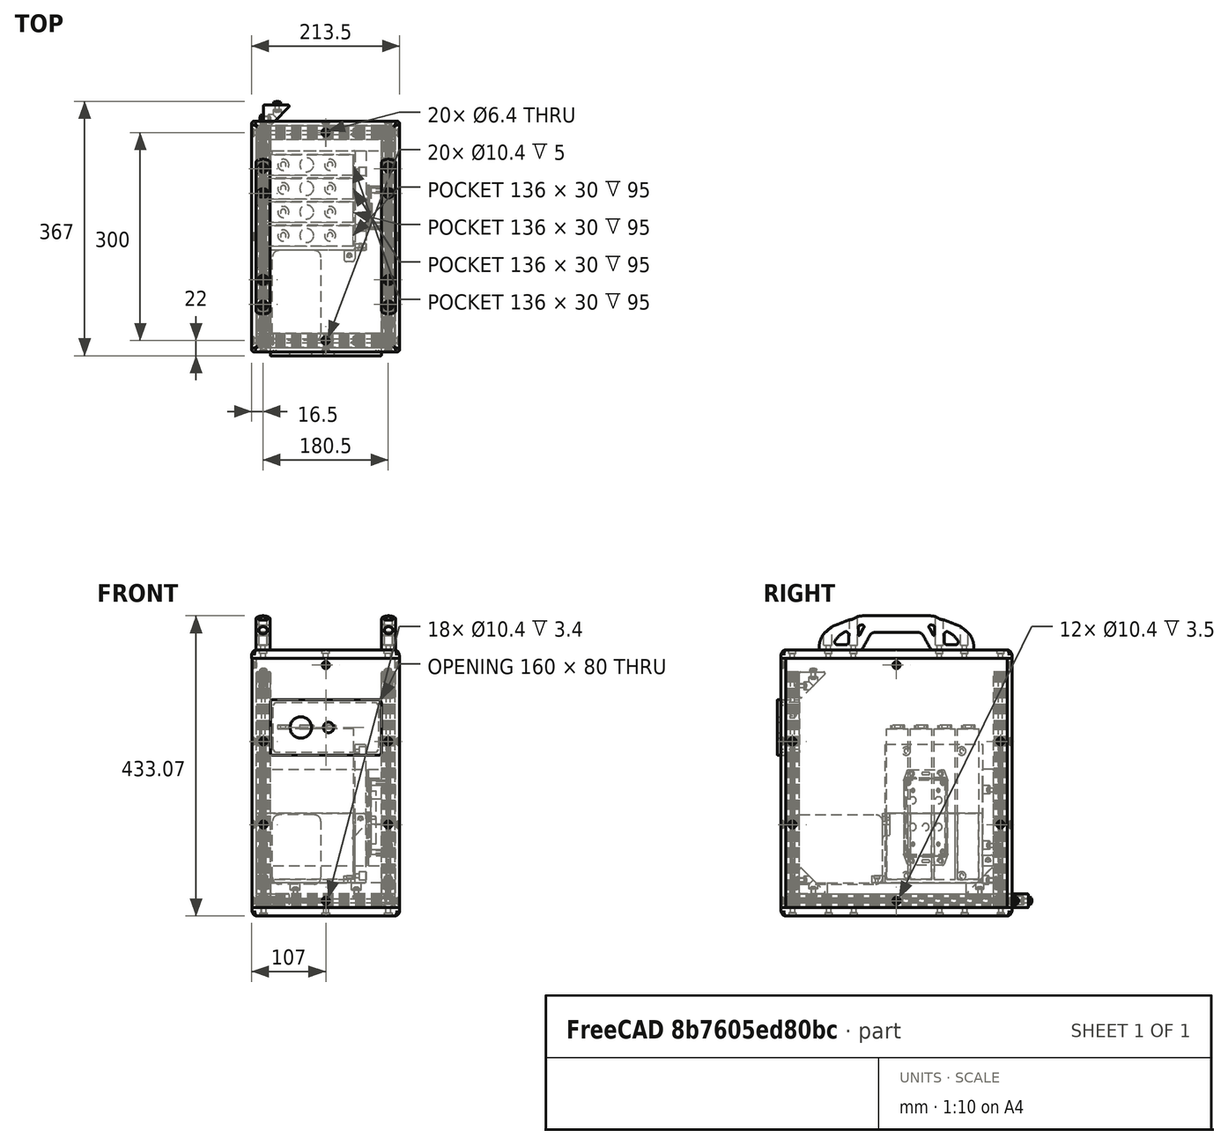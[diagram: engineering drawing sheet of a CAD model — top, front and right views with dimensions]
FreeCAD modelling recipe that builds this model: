
FCSTD DOCUMENT  (FreeCAD 0.17R9796 (Git))
Label: UPKframeNG2j
License: All rights reserved
LicenseURL: http://en.wikipedia.org/wiki/All_rights_reserved
objects: Part::Feature×74, Part::FeaturePython×24, Part::Compound×12, App::FeaturePython×8, App::Part×6, Part::Cylinder×5, Part::Box×4, Part::Cut×4, PartDesign::Body×2, PartDesign::Pocket×1, Part::Fillet×1, Part::MultiFuse×1
note: 129 computed .brp shape members not serialized (recipe doc carries the construction recipe); baked Part::Feature solids carry a one-line shape summary decoded from their .brp

FEATURE [Part::Feature] Pocket003001  label="tslot32con"
  Placement = pos=(0,10,10) rot=(1,0,0;1.5708rad)
  shape: bbox 20 x 320 x 20 mm, 150 faces (baked)
FEATURE [Part::Feature] Pocket003002  label="tslot16"
  Placement = pos=(10,0,10) rot=(0,1,0;1.5708rad)
  shape: bbox 160 x 20 x 20 mm, 94 faces (baked)
FEATURE [Part::Feature] Pocket003006  label="tslot16_001"
  Placement = pos=(10,-300,10) rot=(0,1,0;1.5708rad)
  shape: bbox 160 x 20 x 20 mm, 94 faces (baked)
FEATURE [Part::Feature] Pocket003007  label="tslot32con_001"
  Placement = pos=(180,-310,10) rot=(0,0.707107,0.707107;3.14159rad)
  shape: bbox 20 x 320 x 20 mm, 150 faces (baked)
FEATURE [Part::FeaturePython] Screw  label="M6x25-Screw"  # Fasteners workbench fastener (typed FeaturePython)
  Placement = pos=(-4,0,10) rot=(0,-1,0;1.5708rad)
  diameter = 7
  invert = false
  length = 6
  matchOuter = false
  offset = 0
  thread = false
  type = 15
FEATURE [Part::FeaturePython] Screw001  label="M6x25-Screw004"  # Fasteners workbench fastener (typed FeaturePython)
  Placement = pos=(-4,-300,10) rot=(0,-1,0;1.5708rad)
  diameter = 7
  invert = false
  length = 6
  matchOuter = false
  offset = 0
  thread = false
  type = 15
FEATURE [Part::FeaturePython] Screw002  label="M6x25-Screw005"  # Fasteners workbench fastener (typed FeaturePython)
  Placement = pos=(184,0,10) rot=(0,1,0;1.5708rad)
  diameter = 7
  invert = false
  length = 6
  matchOuter = false
  offset = 0
  thread = false
  type = 15
FEATURE [Part::FeaturePython] Screw004  label="M6x25-Screw006"  # Fasteners workbench fastener (typed FeaturePython)
  Placement = pos=(184,-300,10) rot=(0,1,0;1.5708rad)
  diameter = 7
  invert = false
  length = 6
  matchOuter = false
  offset = 0
  thread = false
  type = 15
FEATURE [App::Part] Part  label="lower_frame"
  Group = -> [Pocket003001,Pocket003002,Pocket003006,Pocket003007,Screw,Screw001,Screw002,Screw004]
  License = CC BY 3.0
  LicenseURL = http://creativecommons.org/licenses/by/3.0/
  Origin = -> PartOrigin
FEATURE [Part::Feature] Pocket003008  label="tslot32con001"
  Placement = pos=(0,10,10) rot=(1,0,0;1.5708rad)
  shape: bbox 20 x 320 x 20 mm, 150 faces (baked)
FEATURE [Part::Feature] Pocket003009  label="tslot041"
  Placement = pos=(10,0,10) rot=(0,1,0;1.5708rad)
  shape: bbox 160 x 20 x 20 mm, 94 faces (baked)
FEATURE [Part::Feature] Pocket003010  label="tslot16_002"
  Placement = pos=(10,-300,10) rot=(0,1,0;1.5708rad)
  shape: bbox 160 x 20 x 20 mm, 94 faces (baked)
FEATURE [Part::Feature] Pocket003011  label="tslot32con_002"
  Placement = pos=(180,-310,10) rot=(0,0.707107,0.707107;3.14159rad)
  shape: bbox 20 x 320 x 20 mm, 150 faces (baked)
FEATURE [Part::FeaturePython] Screw005  label="M6x25-Screw007"  # Fasteners workbench fastener (typed FeaturePython)
  Placement = pos=(-4,0,10) rot=(0,-1,0;1.5708rad)
  diameter = 7
  invert = false
  length = 6
  matchOuter = false
  offset = 0
  thread = false
  type = 15
FEATURE [Part::FeaturePython] Screw006  label="M6x25-Screw008"  # Fasteners workbench fastener (typed FeaturePython)
  Placement = pos=(-4,-300,10) rot=(0,-1,0;1.5708rad)
  diameter = 7
  invert = false
  length = 6
  matchOuter = false
  offset = 0
  thread = false
  type = 15
FEATURE [Part::FeaturePython] Screw007  label="M6x25-Screw009"  # Fasteners workbench fastener (typed FeaturePython)
  Placement = pos=(184,0,10) rot=(0,1,0;1.5708rad)
  diameter = 7
  invert = false
  length = 6
  matchOuter = false
  offset = 0
  thread = false
  type = 15
FEATURE [Part::FeaturePython] Screw008  label="M6x25-Screw010"  # Fasteners workbench fastener (typed FeaturePython)
  Placement = pos=(184,-300,10) rot=(0,1,0;1.5708rad)
  diameter = 7
  invert = false
  length = 6
  matchOuter = false
  offset = 0
  thread = false
  type = 15
FEATURE [App::Part] Part001  label="upper_frame"
  Group = -> [Pocket003008,Pocket003009,Pocket003010,Pocket003011,Screw005,Screw006,Screw007,Screw008]
  License = CC BY 3.0
  LicenseURL = http://creativecommons.org/licenses/by/3.0/
  Origin = -> PartOrigin001
  Placement = pos=(0,0,340) rot=(0,0,1;0rad)
FEATURE [Part::Feature] Fillet004001  label="Fillet005"
  shape: bbox 37.5 x 37.5 x 20 mm, 26 faces (baked)
FEATURE [Part::FeaturePython] Screw009  label="M6x12-Screw"  # Fasteners workbench fastener (typed FeaturePython)
  Placement = pos=(7,20,10) rot=(0,1,0;1.5708rad)
  diameter = 4
  invert = false
  length = 1
  matchOuter = false
  offset = 0
  thread = false
  type = 20
FEATURE [Part::Feature] Body001  label="m6nutplate"
  Placement = pos=(-1.5,15,5) rot=(0,-1,0;1.5708rad)
  shape: bbox 3 x 10 x 10 mm, 9 faces (baked)
FEATURE [App::Part] Part002  label="cornerstonescrewnut"
  License = CC BY 3.0
  LicenseURL = http://creativecommons.org/licenses/by/3.0/
  Origin = -> PartOrigin002
  Placement = pos=(10,-50,20) rot=(0,-1,0;1.5708rad)
FEATURE [Part::FeaturePython] Screw010  label="M6x12-Screw001"  # Fasteners workbench fastener (typed FeaturePython)
  Placement = pos=(20,33,10) rot=(1,0,0;1.5708rad)
  diameter = 4
  invert = false
  length = 1
  matchOuter = false
  offset = 0
  thread = false
  type = 20
FEATURE [Part::Feature] Body002  label="m6nutplate001"
  Placement = pos=(15,41.5,5) rot=(0.57735,0.57735,0.57735;4.18879rad)
  shape: bbox 10 x 3 x 10 mm, 9 faces (baked)
FEATURE [Part::Feature] Fillet004002  label="Fillet006"
  shape: bbox 37.5 x 37.5 x 20 mm, 26 faces (baked)
FEATURE [Part::FeaturePython] Screw011  label="M6x12-Screw002"  # Fasteners workbench fastener (typed FeaturePython)
  Placement = pos=(7,20,10) rot=(0,1,0;1.5708rad)
  diameter = 4
  invert = false
  length = 1
  matchOuter = false
  offset = 0
  thread = false
  type = 20
FEATURE [Part::Feature] Body003  label="m6nutplate002"
  Placement = pos=(-1.5,15,5) rot=(0,-1,0;1.5708rad)
  shape: bbox 3 x 10 x 10 mm, 9 faces (baked)
FEATURE [Part::FeaturePython] Screw012  label="M6x12-Screw003"  # Fasteners workbench fastener (typed FeaturePython)
  Placement = pos=(20,33,10) rot=(1,0,0;1.5708rad)
  diameter = 4
  invert = false
  length = 1
  matchOuter = false
  offset = 0
  thread = false
  type = 20
FEATURE [Part::Feature] Body004  label="m6nutplate003"
  Placement = pos=(15,41.5,5) rot=(0.57735,0.57735,0.57735;4.18879rad)
  shape: bbox 10 x 3 x 10 mm, 9 faces (baked)
FEATURE [App::Part] Part003  label="cornerstonescrewnut001"
  Group = -> [Body003,Screw011,Fillet004002,Screw012,Body004,PartOrigin002,Body001,Screw009,Fillet004001,Screw010,Body002,Part002]
  License = CC BY 3.0
  LicenseURL = http://creativecommons.org/licenses/by/3.0/
  Origin = -> PartOrigin003
  Placement = pos=(190,-50,20) rot=(0,-1,0;1.5708rad)
FEATURE [Part::Feature] Fillet004003  label="Fillet004005006"
  shape: bbox 37.5 x 37.5 x 20 mm, 26 faces (baked)
FEATURE [Part::FeaturePython] Screw013  label="M6x12-Screw004"  # Fasteners workbench fastener (typed FeaturePython)
  Placement = pos=(7,20,10) rot=(0,1,0;1.5708rad)
  diameter = 4
  invert = false
  length = 1
  matchOuter = false
  offset = 0
  thread = false
  type = 20
FEATURE [Part::Feature] Body005  label="m6nutplate004"
  Placement = pos=(-1.5,15,5) rot=(0,-1,0;1.5708rad)
  shape: bbox 3 x 10 x 10 mm, 9 faces (baked)
FEATURE [Part::FeaturePython] Screw014  label="M6x12-Screw005"  # Fasteners workbench fastener (typed FeaturePython)
  Placement = pos=(20,33,10) rot=(1,0,0;1.5708rad)
  diameter = 4
  invert = false
  length = 1
  matchOuter = false
  offset = 0
  thread = false
  type = 20
FEATURE [Part::Feature] Body006  label="m6nutplate005"
  Placement = pos=(15,41.5,5) rot=(0.57735,0.57735,0.57735;4.18879rad)
  shape: bbox 10 x 3 x 10 mm, 9 faces (baked)
FEATURE [App::Part] Part004  label="cornerstonescrewnut002"
  Group = -> [Body005,Screw013,Fillet004003,Screw014,Body006]
  License = CC BY 3.0
  LicenseURL = http://creativecommons.org/licenses/by/3.0/
  Origin = -> PartOrigin004
  Placement = pos=(-10,-50,340) rot=(0,1,0;1.5708rad)
FEATURE [Part::Feature] Fillet004004  label="Fillet008"
  shape: bbox 37.5 x 37.5 x 20 mm, 26 faces (baked)
FEATURE [Part::FeaturePython] Screw015  label="M6x12-Screw006"  # Fasteners workbench fastener (typed FeaturePython)
  Placement = pos=(7,20,10) rot=(0,1,0;1.5708rad)
  diameter = 4
  invert = false
  length = 1
  matchOuter = false
  offset = 0
  thread = false
  type = 20
FEATURE [Part::Feature] Body007  label="m6nutplate006"
  Placement = pos=(-1.5,15,5) rot=(0,-1,0;1.5708rad)
  shape: bbox 3 x 10 x 10 mm, 9 faces (baked)
FEATURE [Part::FeaturePython] Screw016  label="M6x12-Screw007"  # Fasteners workbench fastener (typed FeaturePython)
  Placement = pos=(20,33,10) rot=(1,0,0;1.5708rad)
  diameter = 4
  invert = false
  length = 1
  matchOuter = false
  offset = 0
  thread = false
  type = 20
FEATURE [Part::Feature] Body008  label="m6nutplate007"
  Placement = pos=(15,41.5,5) rot=(0.57735,0.57735,0.57735;4.18879rad)
  shape: bbox 10 x 3 x 10 mm, 9 faces (baked)
FEATURE [App::Part] Part005  label="cornerstonescrewnut003"
  Group = -> [Body007,Screw015,Fillet004004,Screw016,Body008]
  License = CC BY 3.0
  LicenseURL = http://creativecommons.org/licenses/by/3.0/
  Origin = -> PartOrigin005
  Placement = pos=(170,-50,340) rot=(0,1,0;1.5708rad)
FEATURE [Part::Feature] Body009001  label="m6nutplate010"
  Placement = pos=(-1.5,15,5) rot=(0,-1,0;1.5708rad)
  shape: bbox 3 x 10 x 10 mm, 9 faces (baked)
FEATURE [Part::Feature] Body010001  label="m6nutplate011"
  Placement = pos=(15,41.5,5) rot=(0.57735,0.57735,0.57735;4.18879rad)
  shape: bbox 10 x 3 x 10 mm, 9 faces (baked)
FEATURE [Part::Feature] Screw018001  label="M6x12-Screw010"
  Placement = pos=(20,33,10) rot=(1,0,0;1.5708rad)
  shape: bbox 10.5 x 15.3 x 10.5 mm, 15 faces (baked)
FEATURE [Part::Feature] Screw017001  label="M6x12-Screw011"
  Placement = pos=(7,20,10) rot=(0,1,0;1.5708rad)
  shape: bbox 15.3 x 10.5 x 10.5 mm, 15 faces (baked)
FEATURE [Part::Feature] Fillet004005001  label="Fillet010"
  shape: bbox 37.5 x 37.5 x 20 mm, 26 faces (baked)
FEATURE [Part::Compound] Compound
  Links = -> [Body009001,Fillet004005001,Screw017001,Body010001,Screw018001]
  Placement = pos=(10,-250,340) rot=(0.707107,0,-0.707107;3.14159rad)
FEATURE [Part::Feature] Body010002  label="m6nutplate012"
  Placement = pos=(-1.5,15,5) rot=(0,-1,0;1.5708rad)
  shape: bbox 3 x 10 x 10 mm, 9 faces (baked)
FEATURE [Part::Feature] Body010003  label="m6nutplate013"
  Placement = pos=(15,41.5,5) rot=(0.57735,0.57735,0.57735;4.18879rad)
  shape: bbox 10 x 3 x 10 mm, 9 faces (baked)
FEATURE [Part::Feature] Screw018002  label="M6x12-Screw012"
  Placement = pos=(20,33,10) rot=(1,0,0;1.5708rad)
  shape: bbox 10.5 x 15.3 x 10.5 mm, 15 faces (baked)
FEATURE [Part::Feature] Screw018003  label="M6x12-Screw013"
  Placement = pos=(7,20,10) rot=(0,1,0;1.5708rad)
  shape: bbox 15.3 x 10.5 x 10.5 mm, 15 faces (baked)
FEATURE [Part::Feature] Fillet004005002  label="Fillet011"
  shape: bbox 37.5 x 37.5 x 20 mm, 26 faces (baked)
FEATURE [Part::Compound] Compound001
  Links = -> [Body010002,Fillet004005002,Screw018003,Body010003,Screw018002]
  Placement = pos=(190,-250,340) rot=(0.707107,0,-0.707107;3.14159rad)
FEATURE [Part::Feature] Body010004  label="m6nutplate014"
  Placement = pos=(-1.5,15,5) rot=(0,-1,0;1.5708rad)
  shape: bbox 3 x 10 x 10 mm, 9 faces (baked)
FEATURE [Part::Feature] Body010005  label="m6nutplate015"
  Placement = pos=(15,41.5,5) rot=(0.57735,0.57735,0.57735;4.18879rad)
  shape: bbox 10 x 3 x 10 mm, 9 faces (baked)
FEATURE [Part::Feature] Screw018004  label="M6x12-Screw014"
  Placement = pos=(20,33,10) rot=(1,0,0;1.5708rad)
  shape: bbox 10.5 x 15.3 x 10.5 mm, 15 faces (baked)
FEATURE [Part::Feature] Screw018005  label="M6x12-Screw015"
  Placement = pos=(7,20,10) rot=(0,1,0;1.5708rad)
  shape: bbox 15.3 x 10.5 x 10.5 mm, 15 faces (baked)
FEATURE [Part::Feature] Fillet004005003  label="Fillet012"
  shape: bbox 37.5 x 37.5 x 20 mm, 26 faces (baked)
FEATURE [Part::Compound] Compound002
  Links = -> [Body010004,Fillet004005003,Screw018005,Body010005,Screw018004]
  Placement = pos=(10,-290,60) rot=(0.57735,0.57735,-0.57735;4.18879rad)
FEATURE [Part::Feature] Body010006  label="m6nutplate016"
  Placement = pos=(-1.5,15,5) rot=(0,-1,0;1.5708rad)
  shape: bbox 3 x 10 x 10 mm, 9 faces (baked)
FEATURE [Part::Feature] Body010007  label="m6nutplate017"
  Placement = pos=(15,41.5,5) rot=(0.57735,0.57735,0.57735;4.18879rad)
  shape: bbox 10 x 3 x 10 mm, 9 faces (baked)
FEATURE [Part::Feature] Screw018006  label="M6x12-Screw016"
  Placement = pos=(20,33,10) rot=(1,0,0;1.5708rad)
  shape: bbox 10.5 x 15.3 x 10.5 mm, 15 faces (baked)
FEATURE [Part::Feature] Screw018007  label="M6x12-Screw017"
  Placement = pos=(7,20,10) rot=(0,1,0;1.5708rad)
  shape: bbox 15.3 x 10.5 x 10.5 mm, 15 faces (baked)
FEATURE [Part::Feature] Fillet004005004  label="Fillet013"
  shape: bbox 37.5 x 37.5 x 20 mm, 26 faces (baked)
FEATURE [Part::Compound] Compound003
  Links = -> [Body010006,Fillet004005004,Screw018007,Body010007,Screw018006]
  Placement = pos=(190,-290,60) rot=(0.57735,0.57735,-0.57735;4.18879rad)
FEATURE [Part::Feature] Pocket001001  label="tslot32"
  Placement = pos=(0,0,20) rot=(0,0,1;0rad)
  shape: bbox 20 x 20 x 320 mm, 94 faces (baked)
FEATURE [Part::Feature] Body010008  label="m6nutplate018"
  Placement = pos=(-1.5,15,5) rot=(0,-1,0;1.5708rad)
  shape: bbox 3 x 10 x 10 mm, 9 faces (baked)
FEATURE [Part::Feature] Body010009  label="m6nutplate019"
  Placement = pos=(15,41.5,5) rot=(0.57735,0.57735,0.57735;4.18879rad)
  shape: bbox 10 x 3 x 10 mm, 9 faces (baked)
FEATURE [Part::Feature] Screw018008  label="M6x12-Screw018"
  Placement = pos=(20,33,10) rot=(1,0,0;1.5708rad)
  shape: bbox 10.5 x 15.3 x 10.5 mm, 15 faces (baked)
FEATURE [Part::Feature] Screw018009  label="M6x12-Screw019"
  Placement = pos=(7,20,10) rot=(0,1,0;1.5708rad)
  shape: bbox 15.3 x 10.5 x 10.5 mm, 15 faces (baked)
FEATURE [Part::Feature] Fillet004005005  label="Fillet014"
  shape: bbox 37.5 x 37.5 x 20 mm, 26 faces (baked)
FEATURE [Part::Compound] Compound004
  Links = -> [Body010008,Fillet004005005,Screw018009,Body010009,Screw018008]
  Placement = pos=(-10,-10,60) rot=(0.57735,-0.57735,0.57735;4.18879rad)
FEATURE [Part::Feature] Pocket003012  label="tslot32_001"
  Placement = pos=(0,-300,20) rot=(0,0,1;0rad)
  shape: bbox 20 x 20 x 320 mm, 94 faces (baked)
FEATURE [Part::Feature] Pocket003013  label="tslot32_002"
  Placement = pos=(180,0,20) rot=(0,0,1;0rad)
  shape: bbox 20 x 20 x 320 mm, 94 faces (baked)
FEATURE [Part::Feature] Pocket003014  label="tslot32_003"
  Placement = pos=(180,-300,20) rot=(0,0,1;0rad)
  shape: bbox 20 x 20 x 320 mm, 94 faces (baked)
FEATURE [PartDesign::Body] Body010027
FEATURE [Part::FeaturePython] Screw018021  label="M6x12-Screw032"  # Fasteners workbench fastener (typed FeaturePython)
  diameter = 4
  invert = false
  length = 1
  matchOuter = false
  offset = 0
  thread = false
  type = 20
FEATURE [Part::Feature] Body010028  label="m6nutplate032"
  Placement = pos=(5,-5,-8.39) rot=(0,1,0;3.14159rad)
  shape: bbox 10 x 10 x 3 mm, 9 faces (baked)
FEATURE [App::FeaturePython] circularEdgeConstraint009  # a2plus constraint (typed FeaturePython)
  Object1 = Screw
  Object2 = Body001
  SubElement1 = Edge7
  SubElement2 = Edge20
  Type = circularEdge
  directionConstraint = 1
  lockRotation = false
  offset = 0
FEATURE [Part::Compound] Compound017  label="nutplate12screw008"
  Links = -> [Screw018021,circularEdgeConstraint009,Body010028]
  Placement = pos=(10,30,6) rot=(0,0,1;0rad)
FEATURE [Part::FeaturePython] Screw018022  label="M6x12-Screw033"  # Fasteners workbench fastener (typed FeaturePython)
  diameter = 4
  invert = false
  length = 1
  matchOuter = false
  offset = 0
  thread = false
  type = 20
FEATURE [Part::Feature] Body010029  label="m6nutplate033"
  Placement = pos=(5,-5,-8.39) rot=(0,1,0;3.14159rad)
  shape: bbox 10 x 10 x 3 mm, 9 faces (baked)
FEATURE [App::FeaturePython] circularEdgeConstraint010  # a2plus constraint (typed FeaturePython)
  Object1 = Screw
  Object2 = Body001
  SubElement1 = Edge7
  SubElement2 = Edge20
  Type = circularEdge
  directionConstraint = 1
  lockRotation = false
  offset = 0
FEATURE [Part::Compound] Compound018  label="nutplate12screw009"
  Links = -> [Screw018022,circularEdgeConstraint010,Body010029]
  Placement = pos=(10,110,6) rot=(0,0,1;0rad)
FEATURE [Part::FeaturePython] Screw018023  label="M6x12-Screw034"  # Fasteners workbench fastener (typed FeaturePython)
  diameter = 4
  invert = false
  length = 1
  matchOuter = false
  offset = 0
  thread = false
  type = 20
FEATURE [Part::Feature] Body010030  label="m6nutplate034"
  Placement = pos=(5,-5,-8.39) rot=(0,1,0;3.14159rad)
  shape: bbox 10 x 10 x 3 mm, 9 faces (baked)
FEATURE [App::FeaturePython] circularEdgeConstraint011  # a2plus constraint (typed FeaturePython)
  Object1 = Screw
  Object2 = Body001
  SubElement1 = Edge7
  SubElement2 = Edge20
  Type = circularEdge
  directionConstraint = 1
  lockRotation = false
  offset = 0
FEATURE [Part::Compound] Compound019  label="nutplate12screw010"
  Links = -> [Screw018023,circularEdgeConstraint011,Body010030]
  Placement = pos=(190,110,6) rot=(0,0,1;0rad)
FEATURE [Part::FeaturePython] Screw018024  label="M6x12-Screw035"  # Fasteners workbench fastener (typed FeaturePython)
  diameter = 4
  invert = false
  length = 1
  matchOuter = false
  offset = 0
  thread = false
  type = 20
FEATURE [Part::Feature] Body010031  label="m6nutplate035"
  Placement = pos=(5,-5,-8.39) rot=(0,1,0;3.14159rad)
  shape: bbox 10 x 10 x 3 mm, 9 faces (baked)
FEATURE [App::FeaturePython] circularEdgeConstraint012  # a2plus constraint (typed FeaturePython)
  Object1 = Screw
  Object2 = Body001
  SubElement1 = Edge7
  SubElement2 = Edge20
  Type = circularEdge
  directionConstraint = 1
  lockRotation = false
  offset = 0
FEATURE [Part::Compound] Compound020  label="nutplate12screw011"
  Links = -> [Screw018024,circularEdgeConstraint012,Body010031]
  Placement = pos=(190,30,6) rot=(0,0,1;0rad)
FEATURE [Part::Compound] Compound021  label="front_plate"
  Links = -> [Body010027,Compound020,Compound019,Compound017,Compound018]
  Placement = pos=(-10,-10,60) rot=(1,0,0;1.5708rad)
FEATURE [Part::Compound] Compound016  label="bottom_plate"
  Placement = pos=(190,-310,20) rot=(0,0,1;1.5708rad)
FEATURE [PartDesign::Pocket] Pocket003019
  Length = 10
  Placement = pos=(130,-166,235) rot=(0,1,0;1.5708rad)
  Type = 0
FEATURE [Part::Box] Box003  label="MPPT"
  AttacherType = Attacher::AttachEngine3D
  Height = 100
  Length = 130
  Placement = pos=(290,128,10) rot=(0,0,1;0rad)
  Width = 70
FEATURE [Part::Fillet] Fillet007  label="MPPT               "
  Base = -> Box003
  Edges = 12 edges r=10: [Edge1,Edge2,Edge3,Edge4,Edge5,Edge6,Edge7,Edge8,Edge9,Edge10,Edge11,Edge12]
  Placement = pos=(211,-590,24) rot=(0,0,1;1.5708rad)
FEATURE [Part::Feature] Part__Feature1213  label="1591XXBF LID"
  Placement = pos=(153,-86,180) rot=(0.57735,-0.57735,-0.57735;2.0944rad)
  shape: bbox 12.61 x 63.32 x 138 mm, 220 faces (baked)
FEATURE [Part::Feature] Part__Feature1212  label="1591XXB BOX"
  Placement = pos=(0,0,0) rot=(0,0.707107,0.707107;3.14159rad)
  shape: bbox 113.8 x 28.25 x 63.32 mm, 133 faces (baked)
FEATURE [Part::Cylinder] Cylinder  label="Zylinder"
  Angle = 360
  AttacherType = Attacher::AttachEngine3D
  Height = 60
  Placement = pos=(-14,48,18.6) rot=(1,0,0;1.5708rad)
  Radius = 5
FEATURE [Part::Cylinder] Cylinder001  label="Zylinder001"
  Angle = 360
  AttacherType = Attacher::AttachEngine3D
  Height = 60
  Placement = pos=(-14,48,0) rot=(1,0,0;1.5708rad)
  Radius = 5
FEATURE [Part::Cylinder] Cylinder002  label="Zylinder002"
  Angle = 360
  AttacherType = Attacher::AttachEngine3D
  Height = 60
  Placement = pos=(-14,48,-18.66) rot=(1,0,0;1.5708rad)
  Radius = 5
FEATURE [Part::Cylinder] Cylinder003  label="Zylinder003"
  Angle = 360
  AttacherType = Attacher::AttachEngine3D
  Height = 60
  Placement = pos=(24.49,48,18.6) rot=(1,0,0;1.5708rad)
  Radius = 5
FEATURE [Part::Cylinder] Cylinder004  label="Zylinder004"
  Angle = 360
  AttacherType = Attacher::AttachEngine3D
  Height = 60
  Placement = pos=(24.49,48,-18.66) rot=(1,0,0;1.5708rad)
  Radius = 5
FEATURE [Part::MultiFuse] Fusion
  Shapes = -> [Cylinder,Cylinder004,Cylinder003,Cylinder002,Cylinder001]
FEATURE [Part::Cut] Cut
  Base = -> Part__Feature1212
  Tool = -> Fusion
FEATURE [Part::Box] Box002  label="Würfel002"
  AttacherType = Attacher::AttachEngine3D
  Height = 10
  Length = 76
  Placement = pos=(-38,16,-36) rot=(0,0,1;0rad)
  Width = 12.6
FEATURE [Part::Cut] Cut001
  Base = -> Cut
  Tool = -> Box002
FEATURE [Part::Box] Box004  label="Würfel003"
  AttacherType = Attacher::AttachEngine3D
  Height = 10
  Length = 36
  Placement = pos=(-10,9,24) rot=(0,0,1;0rad)
  Width = 20
FEATURE [Part::Cut] Cut002
  Base = -> Cut001
  Tool = -> Box004
FEATURE [Part::Box] Box  label="Würfel"
  AttacherType = Attacher::AttachEngine3D
  Height = 20
  Length = 10
  Placement = pos=(49,23,-6) rot=(0,0,1;0rad)
  Width = 6
FEATURE [Part::Cut] Cut003  label="bms-cover"
  Base = -> Cut002
  Placement = pos=(179,-108,130.5) rot=(0.57735,-0.57735,0.57735;2.0944rad)
  Tool = -> Box
FEATURE [PartDesign::Body] Body010032
FEATURE [Part::FeaturePython] Screw018025  label="M6x12-Screw036"  # Fasteners workbench fastener (typed FeaturePython)
  diameter = 4
  invert = false
  length = 1
  matchOuter = false
  offset = 0
  thread = false
  type = 20
FEATURE [App::FeaturePython] circularEdgeConstraint013  # a2plus constraint (typed FeaturePython)
  Object1 = Screw
  Object2 = Body001
  SubElement1 = Edge7
  SubElement2 = Edge20
  Type = circularEdge
  directionConstraint = 1
  lockRotation = false
  offset = 0
FEATURE [Part::FeaturePython] Screw018026  label="M6x12-Screw037"  # Fasteners workbench fastener (typed FeaturePython)
  diameter = 4
  invert = false
  length = 1
  matchOuter = false
  offset = 0
  thread = false
  type = 20
FEATURE [Part::Feature] Body010034  label="m6nutplate037"
  Placement = pos=(5,-5,-8.39) rot=(0,1,0;3.14159rad)
  shape: bbox 10 x 10 x 3 mm, 9 faces (baked)
FEATURE [App::FeaturePython] circularEdgeConstraint014  # a2plus constraint (typed FeaturePython)
  Object1 = Screw
  Object2 = Body001
  SubElement1 = Edge7
  SubElement2 = Edge20
  Type = circularEdge
  directionConstraint = 1
  lockRotation = false
  offset = 0
FEATURE [Part::FeaturePython] Screw018027  label="M6x12-Screw038"  # Fasteners workbench fastener (typed FeaturePython)
  diameter = 4
  invert = false
  length = 1
  matchOuter = false
  offset = 0
  thread = false
  type = 20
FEATURE [Part::Feature] Body010035  label="m6nutplate038"
  Placement = pos=(5,-5,-8.39) rot=(0,1,0;3.14159rad)
  shape: bbox 10 x 10 x 3 mm, 9 faces (baked)
FEATURE [App::FeaturePython] circularEdgeConstraint015  # a2plus constraint (typed FeaturePython)
  Object1 = Screw
  Object2 = Body001
  SubElement1 = Edge7
  SubElement2 = Edge20
  Type = circularEdge
  directionConstraint = 1
  lockRotation = false
  offset = 0
FEATURE [Part::FeaturePython] Screw018028  label="M6x12-Screw039"  # Fasteners workbench fastener (typed FeaturePython)
  diameter = 4
  invert = false
  length = 1
  matchOuter = false
  offset = 0
  thread = false
  type = 20
FEATURE [Part::Feature] Body010036  label="m6nutplate039"
  Placement = pos=(5,-5,-8.39) rot=(0,1,0;3.14159rad)
  shape: bbox 10 x 10 x 3 mm, 9 faces (baked)
FEATURE [App::FeaturePython] circularEdgeConstraint016  # a2plus constraint (typed FeaturePython)
  Object1 = Screw
  Object2 = Body001
  SubElement1 = Edge7
  SubElement2 = Edge20
  Type = circularEdge
  directionConstraint = 1
  lockRotation = false
  offset = 0
FEATURE [Part::Compound] Compound026  label="bmsmounting_plate"
  Links = -> [Body010032]
  Placement = pos=(132,-26,36) rot=(0.707107,0,0.707107;3.14159rad)
FEATURE [Part::Feature] Body010037  label="batterymount"
  Placement = pos=(-10,-170,36) rot=(0,0,1;0rad)
  shape: bbox 158 x 176 x 100 mm, 72 faces (baked)
FEATURE [Part::Feature] Body010033  label="m6nutplate036"
  Placement = pos=(5,-5,-8.39) rot=(0,1,0;3.14159rad)
  shape: bbox 10 x 10 x 3 mm, 9 faces (baked)
FEATURE [Part::Feature] Body010038  label="cam72"
  Placement = pos=(130,-62,41) rot=(0,0,1;1.5708rad)
  shape: bbox 135.1 x 31 x 222.5 mm, 16 faces (baked)
FEATURE [Part::Feature] Body010039  label="cam72_001"
  Placement = pos=(130,-96,41) rot=(0,0,1;1.5708rad)
  shape: bbox 135.1 x 31 x 222.5 mm, 16 faces (baked)
FEATURE [Part::Feature] Body010040  label="cam72_002"
  Placement = pos=(130,-130,41) rot=(0,0,1;1.5708rad)
  shape: bbox 135.1 x 31 x 222.5 mm, 16 faces (baked)
FEATURE [Part::Feature] Body010041  label="cam72_003"
  Placement = pos=(130,-164,41) rot=(0,0,1;1.5708rad)
  shape: bbox 135.1 x 31 x 222.5 mm, 16 faces (baked)
FEATURE [Part::Feature] Body010042  label="backCover"
  Placement = pos=(-16.5,-310,0) rot=(1,0,0;1.5708rad)
  shape: bbox 213 x 6.5 x 360 mm, 26 faces (baked)
FEATURE [Part::Feature] Body010043  label="frontCover"
  Placement = pos=(196.5,10,0) rot=(0,0.707107,0.707107;3.14159rad)
  shape: bbox 213 x 6.5 x 360 mm, 26 faces (baked)
FEATURE [Part::Feature] Body010044  label="topCover"
  Placement = pos=(-17,-316.5,360) rot=(0,0,1;0rad)
  shape: bbox 213 x 333 x 12 mm, 48 faces (baked)
FEATURE [Part::Feature] Body010045  label="bottomCover"
  Placement = pos=(196.5,-316.5,0) rot=(0,1,0;3.14159rad)
  shape: bbox 213 x 333 x 12 mm, 48 faces (baked)
FEATURE [Part::Feature] Pocket003020  label="sideCover"
  Placement = pos=(190,-310,0) rot=(0.57735,0.57735,0.57735;2.0944rad)
  shape: bbox 6.5 x 320 x 360 mm, 24 faces (baked)
FEATURE [Part::Feature] Pocket003021  label="sideCover001"
  Placement = pos=(-10,10,0) rot=(0.57735,-0.57735,-0.57735;2.0944rad)
  shape: bbox 6.5 x 320 x 360 mm, 24 faces (baked)
FEATURE [Part::Feature] Cut007001  label="handle"
  Placement = pos=(7,-150,372) rot=(0.57735,-0.57735,-0.57735;2.0944rad)
  shape: bbox 20 x 223 x 50.93 mm, 233 faces (baked)
FEATURE [Part::Feature] Cut007002  label="handle001"
  Placement = pos=(188,-150,372) rot=(0.57735,-0.57735,-0.57735;2.0944rad)
  shape: bbox 20 x 223 x 50.93 mm, 233 faces (baked)
FEATURE [Part::Feature] Body010046  label="backCover_ifmount"
  Placement = pos=(-16.5,-310,0) rot=(1,0,0;1.5708rad)
  shape: bbox 213 x 6.5 x 360 mm, 34 faces (baked)
FEATURE [Part::Feature] Body010047  label="ifmount"
  Placement = pos=(10,-322,300) rot=(-1,0,0;1.5708rad)
  shape: bbox 160.7 x 32 x 80.66 mm, 41 faces (baked)
